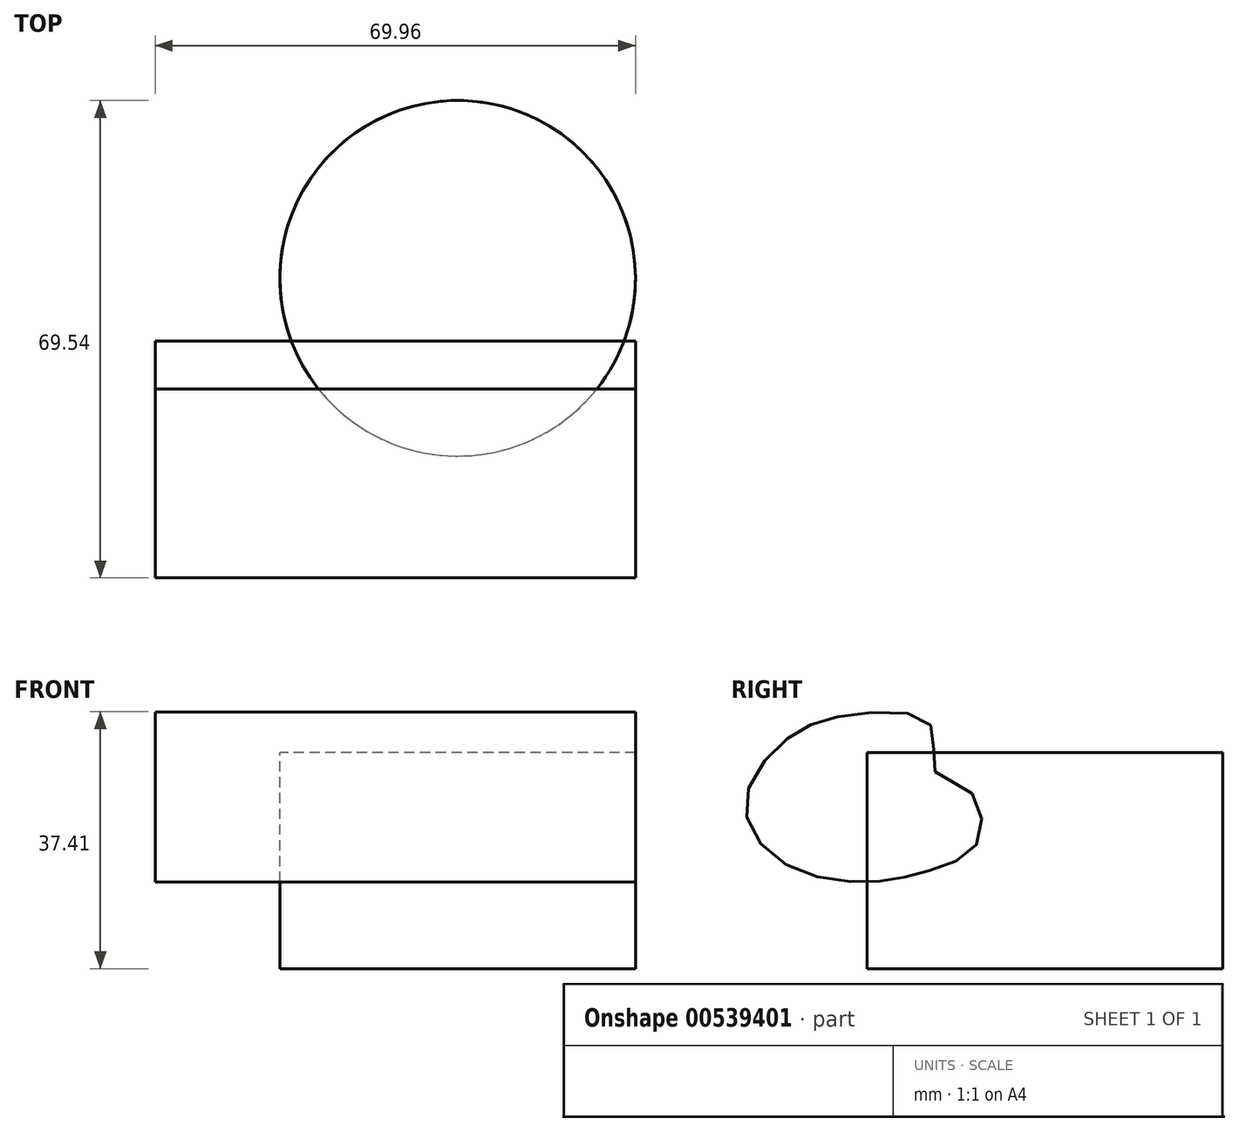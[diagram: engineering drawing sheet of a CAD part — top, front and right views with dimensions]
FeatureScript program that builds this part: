
annotation { "Feature Type Name" : "Feature", "Feature Type Description" : "" }
export const myFeature = defineFeature(function(context is Context, id is Id, definition is map)
    precondition{}
    {
        {
            var Q0;
            Q0=qCreatedBy(makeId("Top.planeOp"),FACE);
            var sketch = newSketch(context, id + "F0", { "sketchPlane" : qUnion([Q0])});
            skCircle(sketch, "E0", {"center": v(-25.9, 0) * mm, "radius": 25.9 * mm});
            skSolve(sketch);
        }
        {
            var Q0;
            Q0=sQuery(id+"F0.wireOp",EDGE,"E0");
            extrude(context, id + "F1", {"bodyType" : ToolBodyType.SURFACE, "surfaceEntities" : qUnion([Q0]), "depth" : 31.44 * mm, "offsetDistance" : 25.4 * mm});
        }
        {
            var Q0;
            Q0=qCreatedBy(makeId("Right.planeOp"),FACE);
            var sketch = newSketch(context, id + "F2", { "sketchPlane" : qUnion([Q0])});
            skFitSpline(sketch, "E1", {"points": [v(-16.6, 35.48) * mm, v(-28.45, 36.96) * mm, v(-37.43, 33.57) * mm, v(-43.63, 23.95) * mm, v(-37.52, 15.06) * mm, v(-24.96, 12.65) * mm, v(-17.34, 14.16) * mm, v(-9.68, 18.5) * mm, v(-11.28, 26.17) * mm, v(-16, 28.74) * mm, v(-16.6, 35.48) * mm]});
            skSolve(sketch);
        }
        {
            var Q0;
            Q0=sQuery(id+"F2.wireOp",EDGE,"E1");
            extrude(context, id + "F3", {"bodyType" : ToolBodyType.SURFACE, "surfaceEntities" : qUnion([Q0]), "oppositeDirection" : true, "depth" : 69.96 * mm, "offsetDistance" : 25.4 * mm});
        }
    });
